# Revit family: CAMDEN TOP FIX
name_source: partatom
category: Generic Models
units: mm (PartAtom-declared; Revit-internal decimal feet)

## family parameters
Always vertical = Yes
Can host rebar = No
Cut with Voids When Loaded = No
Part Type = Normal
Room Calculation Point = No
Round Connector Dimension = Use Diameter
Shared = No
Work Plane-Based = No

## types (5) — shared parameters
Keynote = UNEX SYSTEMS, CAMDEN TOP FIX BALUSTRADE
Manufacturer = UNEX SYSTEMS
Max Post Spacing = 1000 mm  [stored 3.28084 ft]
Top Rail Height = 24 mm  [stored 0.0787402 ft]
URL = WWW.UNEX.CO.NZ
zero-valued in all types: Default Elevation

## per-type parameters (varying)
| type | ART TOP RAIL | Description | HEIGHT | LENGTH | Model | PPR TOP RAIL | Pannel QTY | Post Height | Post QTY | VRE TOP RAIL | VRR TOP RAIL | VRT TOP RAIL |
| CAMDEN WITH VRE | No | UNEX CAMDEN FRAMED GLASS WITH VRE TOP RAIL | 1100 mm | 2100 mm | UNEX, CAMDEN TOP FIX (VRE) | No | 2 | 1076 mm  [stored 3.53018 ft] | 3 | Yes | No | No |
| CAMDEN WITH PRR | No | UNEX CAMDEN FRAMED GLASS WITH PRR TOP RAIL | 1250 mm  [stored 4.10105 ft] | 3652 mm | UNEX, CAMDEN TOP FIX (PRR) | Yes | 4 | 1226 mm  [stored 4.02231 ft] | 5 | No | No | No |
| CAMDEN WITH ART | Yes | UNEX CAMDEN FRAMED GLASS WITH ART TOP RAIL | 1200 mm  [stored 3.93701 ft] | 2652 mm  [stored 8.70079 ft] | UNEX, CAMDEN TOP FIX (ART) | No | 3 | 1176 mm  [stored 3.85827 ft] | 4 | No | No | No |
| CAMDEN WITH VRT | No | UNEX CAMDEN FRAMED GLASS WITH VRT TOP RAIL

UNEX CAMDEN FRAMED GLASS WITH…… TOP RAIL

UNEX CAMDEN FRAMED GLASS WITHVRT TOP RAIL | 1200 mm  [stored 3.93701 ft] | 4500 mm | UNEX, CAMDEN TOP FIX (VRT) | No | 5 | 1176 mm  [stored 3.85827 ft] | 6 | No | No | Yes |
| CAMDEN WITH VRR | No | UNEX CAMDEN FRAMED GLASS WITH VRR TOP RAIL | 1200 mm  [stored 3.93701 ft] | 2896 mm  [stored 9.50131 ft] | UNEX, CAMDEN TOP FIX (VRR) | No | 3 | 1176 mm  [stored 3.85827 ft] | 4 | No | Yes | No |

note: [stored X ft] marks values corroborated as IEEE doubles in the binary element streams (Revit-internal decimal feet)

## geometry (parser evidence)
native form markers: Sweep x26
no freeform markers — native parametric forms only
